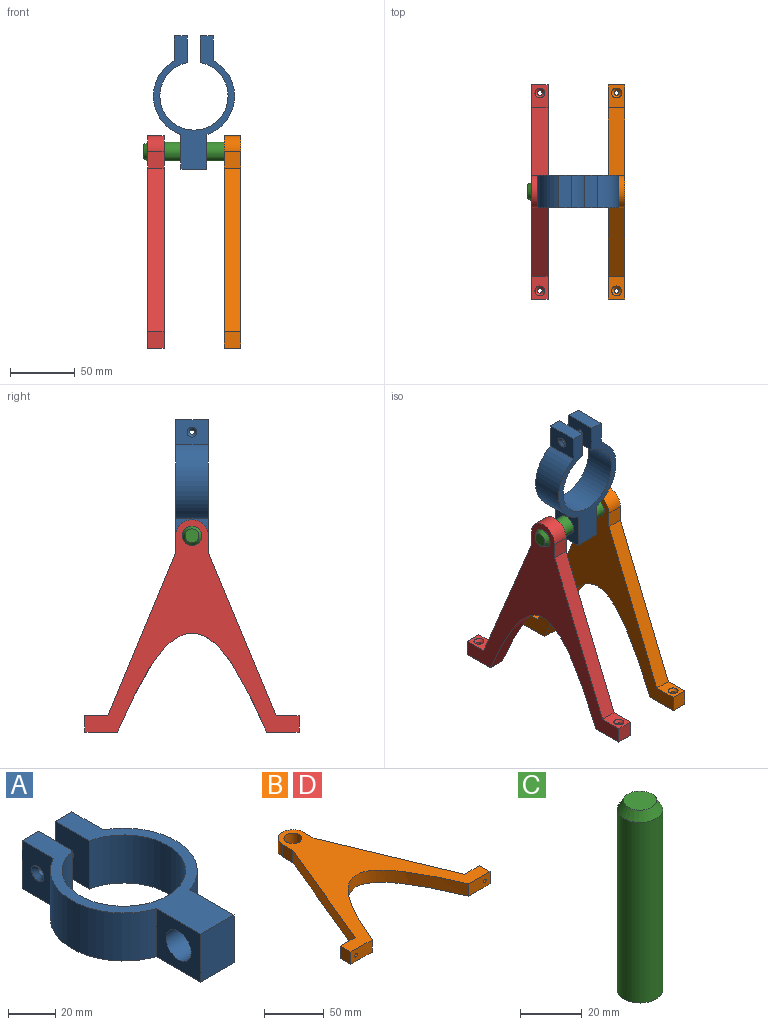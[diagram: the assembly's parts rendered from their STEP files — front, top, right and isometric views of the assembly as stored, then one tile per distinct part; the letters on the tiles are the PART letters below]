
ASSEMBLY  parts=4 mates=3
PART A: 18 faces, bbox 62.5x102.5x25 mm
  f0: cylinder r=26.25mm len=52.5mm, axis (0,0,-1), area 3871.8mm2, adj f1,f11,f12,f13
  f1: plane 25x20.48mm, normal (1,0,0), area 502.4mm2, adj f0,f2,f12,f13,f16
  f2: plane 25x10mm, normal (0,1,0), area 250mm2, adj f1,f3,f12,f13
  f3: plane 25x18.84mm, normal (-1,0,0), area 425.5mm2, adj f2,f4,f12,f13,f17
  f4: cylinder r=31.25mm len=57.02mm, axis (0,0,-1), area 1808.8mm2, adj f3,f5,f12,f13
  f5: plane 26.64x25mm, normal (-1,0,0), area 489.4mm2, adj f4,f6,f12,f13,f14
  f6: plane 25x20mm, normal (0,-1,0), area 500mm2, adj f5,f7,f12,f13
  f7: plane 26.64x25mm, normal (1,0,0), area 489.4mm2, adj f6,f8,f12,f13,f14
  f8: cylinder r=31.25mm len=57.02mm, axis (0,0,-1), area 1808.8mm2, adj f7,f9,f12,f13
  f9: plane 25x18.84mm, normal (1,0,0), area 461.3mm2, adj f8,f10,f12,f13,f15
  f10: plane 25x10mm, normal (0,1,0), area 250mm2, adj f9,f11,f12,f13
  f11: plane 25x20.48mm, normal (-1,0,0), area 502.4mm2, adj f0,f10,f12,f13,f15
  f12: plane 102.5x62.5mm, normal (0,0,1), area 1699.8mm2, adj f0,f1,f2,f3,f4,f5,f6,f7
  f13: plane 102.5x62.5mm, normal (0,0,-1), area 1699.8mm2, adj f0,f1,f2,f3,f4,f5,f6,f7
  f14: cylinder r=7.5mm len=20mm, axis (-1,0,0), area 942.5mm2, adj f5,f7
  f15: cylinder r=1.75mm len=10mm, axis (-1,0,0), area 110mm2, adj f9,f11
  f16: cylinder r=1.75mm len=7.95mm, axis (-1,0,0), area 87.4mm2, adj f1,f17
  f17: cone r=1.75mm half-angle=45deg, axis (-1,0,0), area 50.5mm2, adj f3,f16
PART B: 19 faces, bbox 164.8x181.1x13.8 mm
  f0: plane 126.08x52.23mm, normal (-0.92,0.38,0), area 1705.9mm2, adj f1,f9,f10,f11
  f1: plane 17.68x12.5mm, normal (0,1,0), area 175.6mm2, adj f0,f2,f10,f11,f18
  f2: plane 12.5x12.5mm, normal (-1,0,0), area 156.2mm2, adj f1,f3,f10,f11
  f3: plane 25.07x12.5mm, normal (0,-1,0), area 303.7mm2, adj f2,f10,f11,f13,f16
  f4: plane 25.07x12.5mm, normal (0,-1,0), area 303.7mm2, adj f5,f10,f11,f13,f15
  f5: plane 12.5x12.5mm, normal (1,0,0), area 156.2mm2, adj f4,f6,f10,f11
  f6: plane 17.68x12.5mm, normal (0,1,0), area 175.6mm2, adj f5,f7,f10,f11,f17
  f7: plane 126.08x52.23mm, normal (0.92,0.38,0), area 1705.9mm2, adj f6,f8,f10,f11
  f8: plane 12.5x12.5mm, normal (1,0,0), area 156.2mm2, adj f7,f10,f11,f14
  f9: plane 12.5x12.5mm, normal (-1,0,0), area 156.2mm2, adj f0,f10,f11,f14
  f10: plane 164.81x163.59mm, normal (0,0,1), area 6524.9mm2, adj f0,f1,f2,f3,f4,f5,f6,f7
  f11: plane 164.81x163.59mm, normal (0,0,-1), area 6526.4mm2, adj f0,f1,f2,f3,f4,f5,f6,f7
  f12: cylinder r=7.5mm len=15mm, axis (0,0,1), area 589mm2, adj f10,f11
  f13: bspline ~129.34x106.17mm, area 2479.5mm2, adj f3,f4,f10,f11
  f14: cylinder r=12.5mm len=25mm, axis (0,0,1), area 490.9mm2, adj f8,f9,f10,f11
  f15: cylinder r=1.75mm len=10.45mm, axis (0,1,0), area 114.9mm2, adj f4,f17
  f16: cylinder r=1.75mm len=10.45mm, axis (0,1,0), area 114.9mm2, adj f3,f18
  f17: cone r=1.75mm half-angle=45deg, axis (0,1,0), area 50.5mm2, adj f6,f15
  f18: cone r=1.75mm half-angle=45deg, axis (0,1,0), area 50.5mm2, adj f1,f16
PART C: 4 faces, bbox 14.8x14.8x75 mm
  f0: cylinder r=7.38mm len=71.54mm, axis (0,0,-1), area 3314.9mm2, adj f2,f3
  f1: plane 10.75x10.75mm, normal (0,0,1), area 90.8mm2, adj f3
  f2: plane 14.75x14.75mm, normal (0,0,-1), area 170.9mm2, adj f0
  f3: cone r=5.38mm half-angle=30deg, axis (0,0,-1), area 160.2mm2, adj f0,f1
PART D: same geometry as B
PLACE A rot(axis=(1,0,0),90deg) t=(112.56,10.03,97.55)mm
PLACE B rot(axis=(0.58,-0.58,-0.58),120deg) t=(148.53,139.81,0.85)mm
PLACE C rot(axis=(0,-1,0),90deg) t=(148.53,-2.47,129.19)mm
PLACE D rot(axis=(0.58,-0.58,-0.58),120deg) t=(89.5,139.81,0.85)mm
MATE cylindrical D.f12 <-> C.f0  axis (-1,0,0) through (77,-2.47,54.62)mm
MATE cylindrical B.f12 <-> C.f0  axis (1,0,0) through (148.53,-2.47,54.62)mm
MATE cylindrical A.f14 <-> C.f0  axis (1,0,0) through (122.56,-2.47,54.62)mm
